# Revit family: Shower-Shower_Door-STERLING-Deluxe-572119_1
name_source: partatom
category: Specialty Equipment
units: mm (PartAtom-declared; Revit-internal decimal feet)

## family parameters
Cut with Voids When Loaded = No
Host = Face
OmniClass Number = 23.31.17.17
OmniClass Title = Shower Enclosures
Part Type = Normal
Room Calculation Point = No
Round Connector Dimension = Use Diameter
Shared = No

## types (1)
- S-Silver
    ADA Compliant = No
    Assembly Code = C1030200
    Date Modified = 01/19/2023
    Default Elevation = 4"
    Description = Bypass Door 65.5 X 36
    Distance = 29 1/4"
    Finish = Sterling-Metal-S-Silver
    Height = 65 11/16"
    Length = 2 1/16"
    Manufacturer = Sterling Co.
    Master Format 2014 = 10 28 19.16
    Master Format 2014 Name = Shower Doors
    Material = Premium Metal Construction
    Model = 572119-3G06-S
    Product Documentation Link = https://resources.kohler.com
    Product Name = Deluxe
    Product Page URL = http://www.sterlingplumbing.com
    Type = 1
    URL = https://www.sterlingplumbing.com
    Walk Through = 25 1/16"
    WaterSense Certified = No
    Width = 36"

## geometry (parser evidence)
native form markers: Sweep x5
no freeform markers — native parametric forms only
